# Revit family: Double_Check_Valve_Assemblies-LessShutoff-WATTS-LF709_Series
name_source: partatom
category: Pipe Accessories
revit_build: Autodesk Revit 2016 (Build: 20150714_1515(x64)
units: mm (PartAtom-declared; Revit-internal decimal feet)

## family parameters
Always vertical = Yes
Cut with Voids When Loaded = No
OmniClass Number = 23.65.55.14.21
OmniClass Title = Non-Return Valves for Liquid Services
Part Type = Valve - Breaks Into
Round Connector Dimension = Use Radius
Shared = Yes
Work Plane-Based = No

## types (6) — shared parameters
Assembly Code = F1050
Country = Australia
Description = Lead Free Double Check Valve Assembly.
Manufacturer = WATTS
Manufacturer Product Line = Backflow Prevention
Material = Metal-WATTS-Epoxy Coated Cast Iron
Model = 709
Price = Prices may vary. Please consult Manufacturer Representative for most up-to-date price list.
Product Documentation Link = http://www.wattswater.com.au
Product Page URL = http://www.wattswater.com.au
Region = Oceania
URL = http://www.watts.com
Warranty Information = 1 Year (Limited)

## per-type parameters (varying)
| type | Connection Inlet Description | Connection Outlet Description | Connection Radius | Connection Size | Inlet Radius | Nominal Diameter | Nominal Length | Nominal Width | Radius | Width |
| 709-2.5" | 2 1/2" Inlet Connection | 2 1/2" Outlet Connection | 1 1/4" | 2 1/2" | 1 1/4" | 4 15/16" | 24 1/8" | 2 3/4" | 3 1/2" | 6 5/8" |
| 709-3" | 3" Inlet Connection | 3" Outlet Connection | 1 1/4" | 2 1/2" | 1 1/4" | 4 15/16" | 24 1/8" | 2 3/4" | 3 3/4" | 7 1/8" |
| 709-4" | 4" Inlet Connection | 4" Outlet Connection | 1 1/4" | 2 1/2" | 2" | 7 1/16" | 34 1/8" | 3 1/2" | 4 1/2" | 8 1/8" |
| 709-6" | 6" Inlet Connection | 6" Outlet Connection | 3" | 6" | 3" | 9 29/32" | 41 1/8" | 4 3/4" | 5 1/2" | 9 7/8" |
| 709-8" | 8" Inlet Connection | 8" Outlet Connection | 4" | 8" | 4" | 12 23/32" | 52" | 5 1/2" | 6 1/2" | 10 1/2" |
| 709-10" | 10" Inlet Connection | 10" Outlet Connection | 5" | 10" | 5" | 15 9/16" | 64" | 6 1/4" | 8" | 12" |

## geometry (parser evidence)
native form markers: Sweep x2
no freeform markers — native parametric forms only
